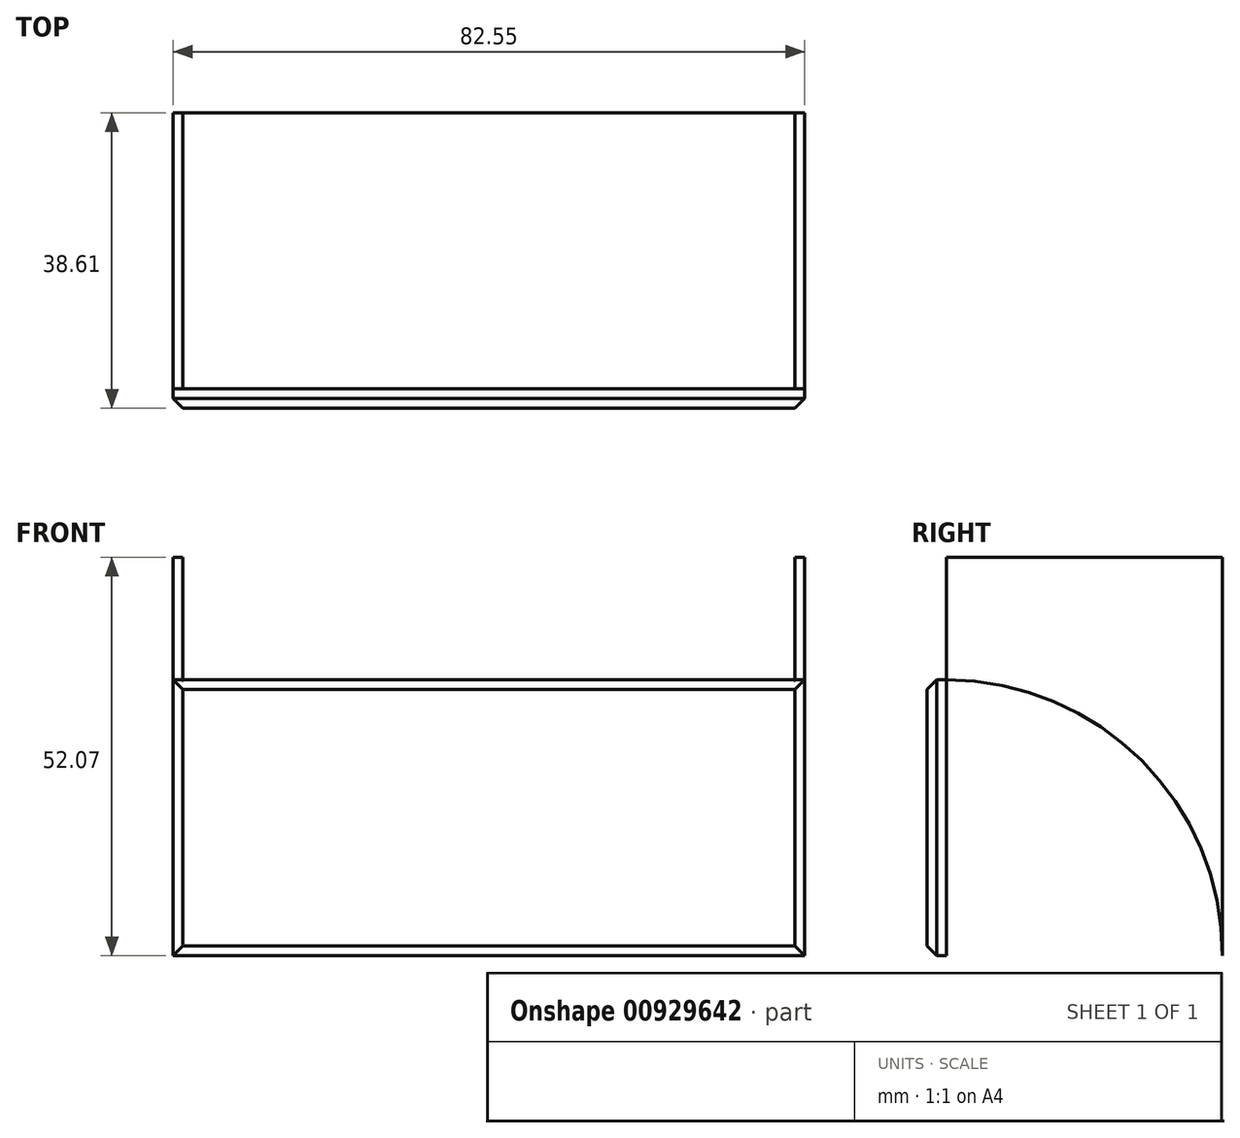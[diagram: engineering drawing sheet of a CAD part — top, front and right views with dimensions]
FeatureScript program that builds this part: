
annotation { "Feature Type Name" : "Feature", "Feature Type Description" : "" }
export const myFeature = defineFeature(function(context is Context, id is Id, definition is map)
    precondition{}
    {
        {
            var Q0;
            Q0=qCreatedBy(makeId("Top.planeOp"),FACE);
            var sketch = newSketch(context, id + "F0", { "sketchPlane" : qUnion([Q0])});
            skLineSegment(sketch, "E0", {"start": v(0, 8.9) * mm, "end": v(89.33, 8.9) * mm, "construction": true});
            skLineSegment(sketch, "E1", {"start": v(0, 27.18) * mm, "end": v(89.33, 27.18) * mm, "construction": true});
            skLineSegment(sketch, "E2", {"start": v(8.9, 0) * mm, "end": v(8.89, 31.45) * mm, "construction": true});
            skLineSegment(sketch, "E3", {"start": v(30.48, 0) * mm, "end": v(30.48, 31.96) * mm, "construction": true});
            skLineSegment(sketch, "E4", {"start": v(52.07, 0) * mm, "end": v(52.07, 32.56) * mm, "construction": true});
            skCircle(sketch, "E5", {"center": v(8.89, 8.9) * mm, "radius": 5.84 * mm});
            skCircle(sketch, "E6", {"center": v(8.89, 27.18) * mm, "radius": 5.84 * mm});
            skCircle(sketch, "E7", {"center": v(30.48, 27.18) * mm, "radius": 5.84 * mm});
            skCircle(sketch, "E8", {"center": v(30.48, 8.9) * mm, "radius": 5.84 * mm});
            skCircle(sketch, "E9", {"center": v(52.07, 8.9) * mm, "radius": 5.84 * mm});
            skCircle(sketch, "E10", {"center": v(52.07, 27.18) * mm, "radius": 5.84 * mm});
            skLineSegment(sketch, "E11", {"start": v(73.66, 0) * mm, "end": v(73.66, 32.56) * mm, "construction": true});
            skCircle(sketch, "E12", {"center": v(73.66, 27.18) * mm, "radius": 5.84 * mm});
            skCircle(sketch, "E13", {"center": v(73.66, 8.9) * mm, "radius": 5.84 * mm});
            skLineSegment(sketch, "E14.bottom", {"start": v(0, 0) * mm, "end": v(82.55, 0) * mm});
            skLineSegment(sketch, "E14.top", {"start": v(0, 36.07) * mm, "end": v(82.55, 36.07) * mm});
            skLineSegment(sketch, "E14.left", {"start": v(0, 0) * mm, "end": v(0, 36.07) * mm});
            skLineSegment(sketch, "E14.right", {"start": v(82.55, 0) * mm, "end": v(82.55, 36.07) * mm});
            skSolve(sketch);
        }
        {
            var Q0;
            Q0=makeQuery(id+"F0.imprint","IMPRINT",FACE,{"disambiguationData":[TD([[makeQuery(id+"F0.imprint","IMPRINT",EDGE,{"derivedFrom":sQuery(id+"F0.wireOp",EDGE,"E5")}),-1.0]])]});
            extrude(context, id + "F1", {"entities" : qUnion([Q0]), "depth" : 1.27 * mm, "offsetDistance" : 25.4 * mm});
        }
        {
            var Q0;
            Q0=makeQuery(id+"F1.opExtrude","CAP_FACE",FACE,{"disambiguationData":[OSD([sQuery(id+"F0.wireOp",EDGE,"E5"),sQuery(id+"F0.wireOp",EDGE,"E6"),sQuery(id+"F0.wireOp",EDGE,"E7"),sQuery(id+"F0.wireOp",EDGE,"E8"),sQuery(id+"F0.wireOp",EDGE,"E9"),sQuery(id+"F0.wireOp",EDGE,"E10"),sQuery(id+"F0.wireOp",EDGE,"E12"),sQuery(id+"F0.wireOp",EDGE,"E13"),sQuery(id+"F0.wireOp",EDGE,"E14.bottom"),sQuery(id+"F0.wireOp",EDGE,"E14.top"),sQuery(id+"F0.wireOp",EDGE,"E14.left"),sQuery(id+"F0.wireOp",EDGE,"E14.right")])],"isStart":false});
            var sketch = newSketch(context, id + "F2", { "sketchPlane" : qUnion([Q0])});
            skLineSegment(sketch, "E15", {"start": v(1.27, 36.07) * mm, "end": v(1.27, 0) * mm});
            skLineSegment(sketch, "E16", {"start": v(81.28, 36.07) * mm, "end": v(81.28, 0) * mm});
            skSolve(sketch);
        }
        {
            var Q0;
            {var subQ0=sQuery(id+"F2.wireOp",EDGE,"E15");Q0=makeQuery(id+"F2.imprint","IMPRINT",FACE,{"disambiguationData":[TD([[makeQuery(id+"F2.imprint","IMPRINT",EDGE,{"derivedFrom":subQ0}),-1.0]])]});}
            var Q1;
            {var subQ0=sQuery(id+"F2.wireOp",EDGE,"E16");Q1=makeQuery(id+"F2.imprint","IMPRINT",FACE,{"disambiguationData":[TD([[makeQuery(id+"F2.imprint","IMPRINT",EDGE,{"derivedFrom":subQ0}),1.0]])]});}
            extrude(context, id + "F3", {"entities" : qUnion([Q0, Q1]), "operationType" : NewBodyOperationType.ADD, "depth" : 50.8 * mm, "offsetDistance" : 25.4 * mm});
        }
        {
            var Q0;
            {var subQ0=sQuery(id+"F0.wireOp",EDGE,"E14.left");Q0=makeQuery(id+"F3.boolean.opBoolean","MERGE",FACE,{"derivedFrom":[makeQuery(id+"F1.opExtrude","SWEPT_FACE",FACE,{"disambiguationData":[OSD([subQ0])]}),makeQuery(id+"F3.opExtrude","SWEPT_FACE",FACE,{"disambiguationData":[OSD([subQ0])]})]});}
            var sketch = newSketch(context, id + "F4", { "sketchPlane" : qUnion([Q0])});
            skArc(sketch, "E17", {"start": v(-36.07, 0) * mm, "mid": v(-25.5, 25.5) * mm, "end": v(0, 36.07) * mm});
            skSolve(sketch);
        }
        {
            var Q0;
            {var subQ0=sQuery(id+"F4.wireOp",EDGE,"E17");Q0=makeQuery(id+"F4.imprint","IMPRINT",FACE,{"disambiguationData":[TD([[makeQuery(id+"F4.imprint","IMPRINT",EDGE,{"derivedFrom":subQ0}),1.0]])]});}
            extrude(context, id + "F5", {"entities" : qUnion([Q0]), "operationType" : NewBodyOperationType.REMOVE, "oppositeDirection" : true, "depth" : 101.6 * mm, "offsetDistance" : 25.4 * mm});
        }
        {
            var Q0;
            {var subQ0=sQuery(id+"F0.wireOp",EDGE,"E14.bottom");var subQ1=makeQuery(id+"F1.opExtrude","CAP_EDGE",EDGE,{"disambiguationData":[OSD([subQ0])],"isStart":false});Q0=makeQuery(id+"F3.boolean.opBoolean","MERGE",FACE,{"derivedFrom":[makeQuery(id+"F1.opExtrude","SWEPT_FACE",FACE,{"disambiguationData":[OSD([subQ0])]}),makeQuery(id+"F3.opExtrude","SWEPT_FACE",FACE,{"disambiguationData":[OSD([subQ0]),TDD([makeQuery(id+"F2.imprint","IMPRINT",EDGE,{"disambiguationData":[TD([[makeQuery(id+"F2.imprint","INTERSECT",VERTEX,{"derivedFrom":[subQ1,makeQuery(id+"F1.opExtrude","CAP_EDGE",EDGE,{"disambiguationData":[OSD([sQuery(id+"F0.wireOp",EDGE,"E14.left")])],"isStart":false})]}),-1.0]])],"derivedFrom":subQ1})])]}),makeQuery(id+"F3.opExtrude","SWEPT_FACE",FACE,{"disambiguationData":[OSD([subQ0]),TDD([makeQuery(id+"F2.imprint","IMPRINT",EDGE,{"disambiguationData":[TD([[makeQuery(id+"F2.imprint","INTERSECT",VERTEX,{"derivedFrom":[subQ1,makeQuery(id+"F1.opExtrude","CAP_EDGE",EDGE,{"disambiguationData":[OSD([sQuery(id+"F0.wireOp",EDGE,"E14.right")])],"isStart":false})]}),1.0]])],"derivedFrom":subQ1})])]})]});}
            var sketch = newSketch(context, id + "F6", { "sketchPlane" : qUnion([Q0])});
            skLineSegment(sketch, "E18.bottom", {"start": v(0, 0) * mm, "end": v(82.55, 0) * mm});
            skLineSegment(sketch, "E18.top", {"start": v(0, 36.07) * mm, "end": v(82.55, 36.07) * mm});
            skLineSegment(sketch, "E18.left", {"start": v(0, 0) * mm, "end": v(0, 36.07) * mm});
            skLineSegment(sketch, "E18.right", {"start": v(82.55, 0) * mm, "end": v(82.55, 36.07) * mm});
            skSolve(sketch);
        }
        {
            var Q0;
            {var subQ1=sQuery(id+"F0.wireOp",EDGE,"E14.bottom");Q0=makeQuery(id+"F6.imprint","IMPRINT",FACE,{"disambiguationData":[TD([[makeQuery(id+"F6.imprint","IMPRINT",EDGE,{"derivedFrom":makeQuery(id+"F1.opExtrude","CAP_EDGE",EDGE,{"disambiguationData":[OSD([subQ1])],"isStart":false})}),1.0]])]});}
            var Q1;
            Q1=makeQuery(id+"F6.imprint","IMPRINT",FACE,{"disambiguationData":[TD([[makeQuery(id+"F6.imprint","IMPRINT",EDGE,{"derivedFrom":sQuery(id+"F6.wireOp",EDGE,"E18.bottom")}),1.0]])]});
            extrude(context, id + "F7", {"entities" : qUnion([Q0, Q1]), "depth" : 2.54 * mm, "offsetDistance" : 25.4 * mm});
        }
        {
            var Q0;
            Q0=makeQuery(id+"F1.opExtrude","SWEPT_BODY",BODY,{"disambiguationData":[OSD([sQuery(id+"F0.wireOp",EDGE,"E5"),sQuery(id+"F0.wireOp",EDGE,"E6"),sQuery(id+"F0.wireOp",EDGE,"E7"),sQuery(id+"F0.wireOp",EDGE,"E8"),sQuery(id+"F0.wireOp",EDGE,"E9"),sQuery(id+"F0.wireOp",EDGE,"E10"),sQuery(id+"F0.wireOp",EDGE,"E12"),sQuery(id+"F0.wireOp",EDGE,"E13"),sQuery(id+"F0.wireOp",EDGE,"E14.bottom"),sQuery(id+"F0.wireOp",EDGE,"E14.top"),sQuery(id+"F0.wireOp",EDGE,"E14.left"),sQuery(id+"F0.wireOp",EDGE,"E14.right")])]});
            var Q1;
            Q1=makeQuery(id+"F7.opExtrude","SWEPT_BODY",BODY,{"disambiguationData":[OSD([sQuery(id+"F6.wireOp",EDGE,"E18.bottom"),sQuery(id+"F6.wireOp",EDGE,"E18.top"),sQuery(id+"F6.wireOp",EDGE,"E18.left"),sQuery(id+"F6.wireOp",EDGE,"E18.right")])]});
            booleanBodies(context, id + "F8", {"operationType" : BooleanOperationType.UNION, "tools" : qUnion([Q0, Q1])});
        }
        {
            var Q0;
            Q0=makeQuery(id+"F7.opExtrude","CAP_EDGE",EDGE,{"disambiguationData":[OSD([sQuery(id+"F6.wireOp",EDGE,"E18.right")])],"isStart":false});
            var Q1;
            Q1=makeQuery(id+"F7.opExtrude","CAP_EDGE",EDGE,{"disambiguationData":[OSD([sQuery(id+"F6.wireOp",EDGE,"E18.top")])],"isStart":false});
            var Q2;
            Q2=makeQuery(id+"F7.opExtrude","CAP_EDGE",EDGE,{"disambiguationData":[OSD([sQuery(id+"F6.wireOp",EDGE,"E18.bottom")])],"isStart":false});
            var Q3;
            Q3=makeQuery(id+"F7.opExtrude","CAP_EDGE",EDGE,{"disambiguationData":[OSD([sQuery(id+"F6.wireOp",EDGE,"E18.left")])],"isStart":false});
            chamfer(context, id + "F9", {"entities" : qUnion([Q0, Q1, Q2, Q3]), "width" : 1.27 * mm, "tangentPropagation" : true});
        }
    });
